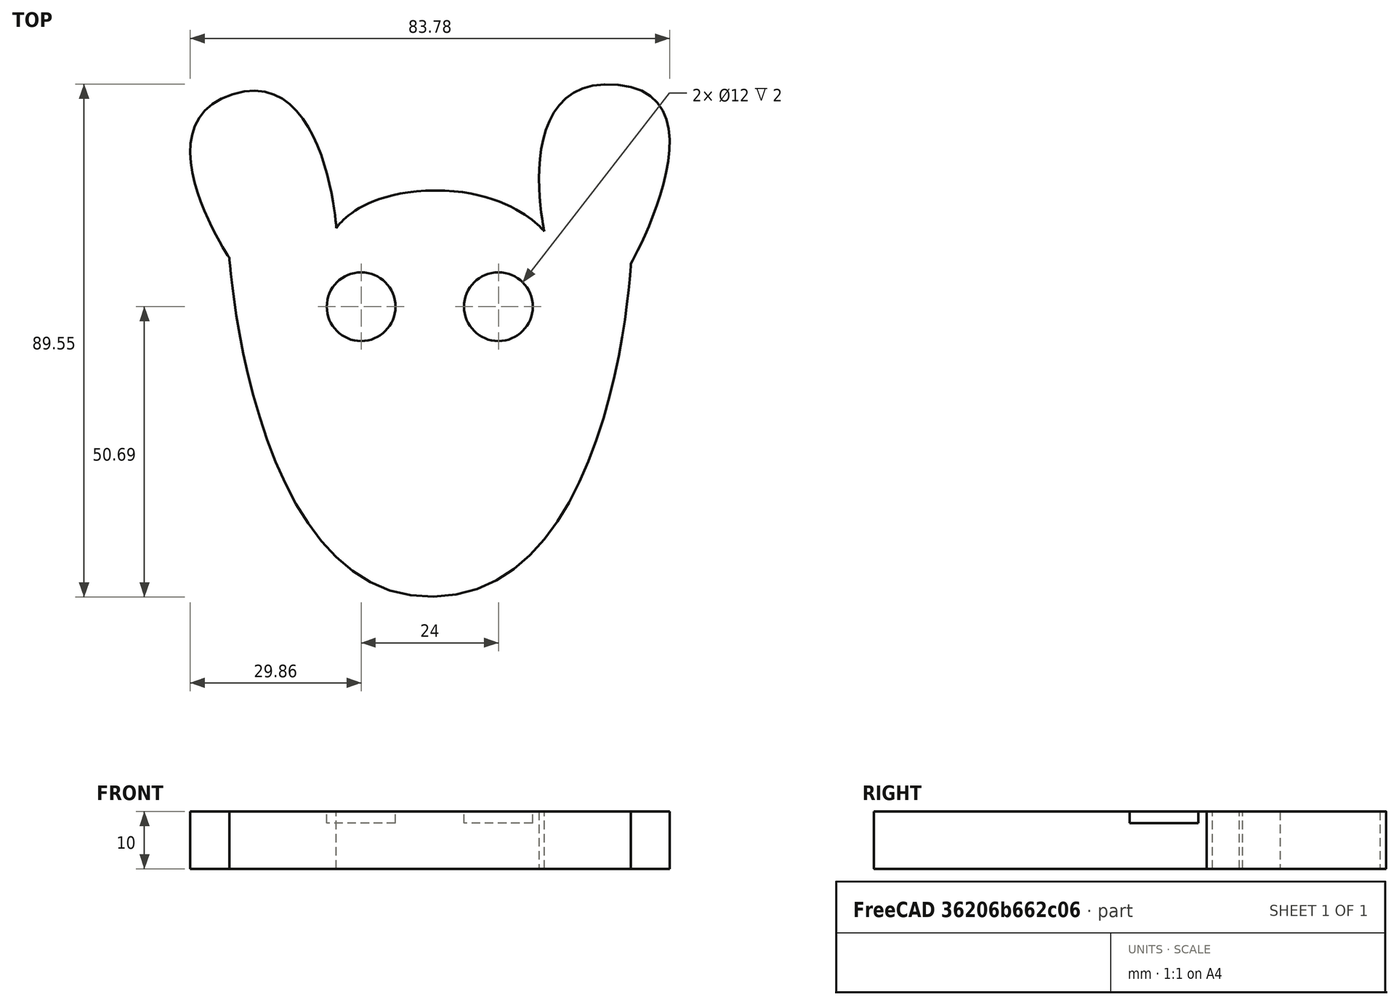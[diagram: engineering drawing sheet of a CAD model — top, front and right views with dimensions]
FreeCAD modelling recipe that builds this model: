
FCSTD DOCUMENT  (FreeCAD 0.17R13217 (Git))
Label: 08-conejo-gato
License: All rights reserved
LicenseURL: http://en.wikipedia.org/wiki/All_rights_reserved
objects: Part::Cylinder×2, Part::Feature×1, Part::Extrusion×1, Part::MultiFuse×1, Part::Cut×1, Sketcher::SketchObject×1
note: 7 computed .brp shape members not serialized (recipe doc carries the construction recipe); baked Part::Feature solids carry a one-line shape summary decoded from their .brp

FEATURE [Part::Feature] path4136
  shape: bbox 91.11 x 91.85 x 2e-07 mm, 0 faces, 0 solids (baked)
FEATURE [Part::Extrusion] Extrude
  Base = -> path4136
  Dir = (0,0,-1)
  DirMode = 2
  FaceMakerClass = Part::FaceMakerBullseye
  LengthFwd = 10
  LengthRev = 0
  Reversed = true
  Solid = true
  Symmetric = false
FEATURE [Part::Cylinder] Cylinder  label="Cilindro"
  Angle = 360
  AttacherType = Attacher::AttachEngine3D
  Height = 10
  Placement = pos=(30,-39,8) rot=(0,0,1;0rad)
  Radius = 6
FEATURE [Part::Cylinder] Cylinder001  label="Cilindro001"
  Angle = 360
  AttacherType = Attacher::AttachEngine3D
  Height = 10
  Placement = pos=(54,-39,8) rot=(0,0,1;0rad)
  Radius = 6
FEATURE [Part::MultiFuse] Fusion
  Refine = true
  Shapes = -> [Cylinder,Cylinder001]
FEATURE [Part::Cut] Cut
  Base = -> Extrude
  Placement = pos=(-42,0,0) rot=(0,0,1;0rad)
  Refine = true
  Tool = -> Fusion
FEATURE [Sketcher::SketchObject] Sketch
  MapMode = 5
  Placement = pos=(-42,0,10) rot=(0,0,1;0rad)
  Support = -> [Cut]
  sketch-geometry (8):
    g0: LineSegment StartX=25.9454 StartY=-62.3199 StartZ=0 EndX=35.4058 EndY=-51.9265 EndZ=0
    g1: LineSegment StartX=35.4058 StartY=-51.9265 StartZ=0 EndX=45.0676 EndY=-59.6915 EndZ=0
    g2: LineSegment StartX=45.0676 StartY=-59.6915 StartZ=0 EndX=53.3204 EndY=-52.9305 EndZ=0
    g3: LineSegment StartX=53.3204 StartY=-52.9305 StartZ=0 EndX=61.5109 EndY=-62.5573 EndZ=0
    g4: LineSegment StartX=61.5109 StartY=-62.5573 StartZ=0 EndX=50.8214 EndY=-76.2598 EndZ=0
    g5: LineSegment StartX=50.8214 StartY=-76.2598 StartZ=0 EndX=41.7054 EndY=-67.9795 EndZ=0
    g6: LineSegment StartX=41.7054 StartY=-67.9795 StartZ=0 EndX=30.8683 EndY=-70.8208 EndZ=0
    g7: LineSegment StartX=30.8683 StartY=-70.8208 StartZ=0 EndX=25.9454 EndY=-62.3199 EndZ=0
  constraints (8):
    c: Coincident(g0,g1)
    c: Coincident(g1,g2)
    c: Coincident(g2,g3)
    c: Coincident(g3,g4)
    c: Coincident(g4,g5)
    c: Coincident(g5,g6)
    c: Coincident(g6,g7)
    c: Coincident(g7,g0)
